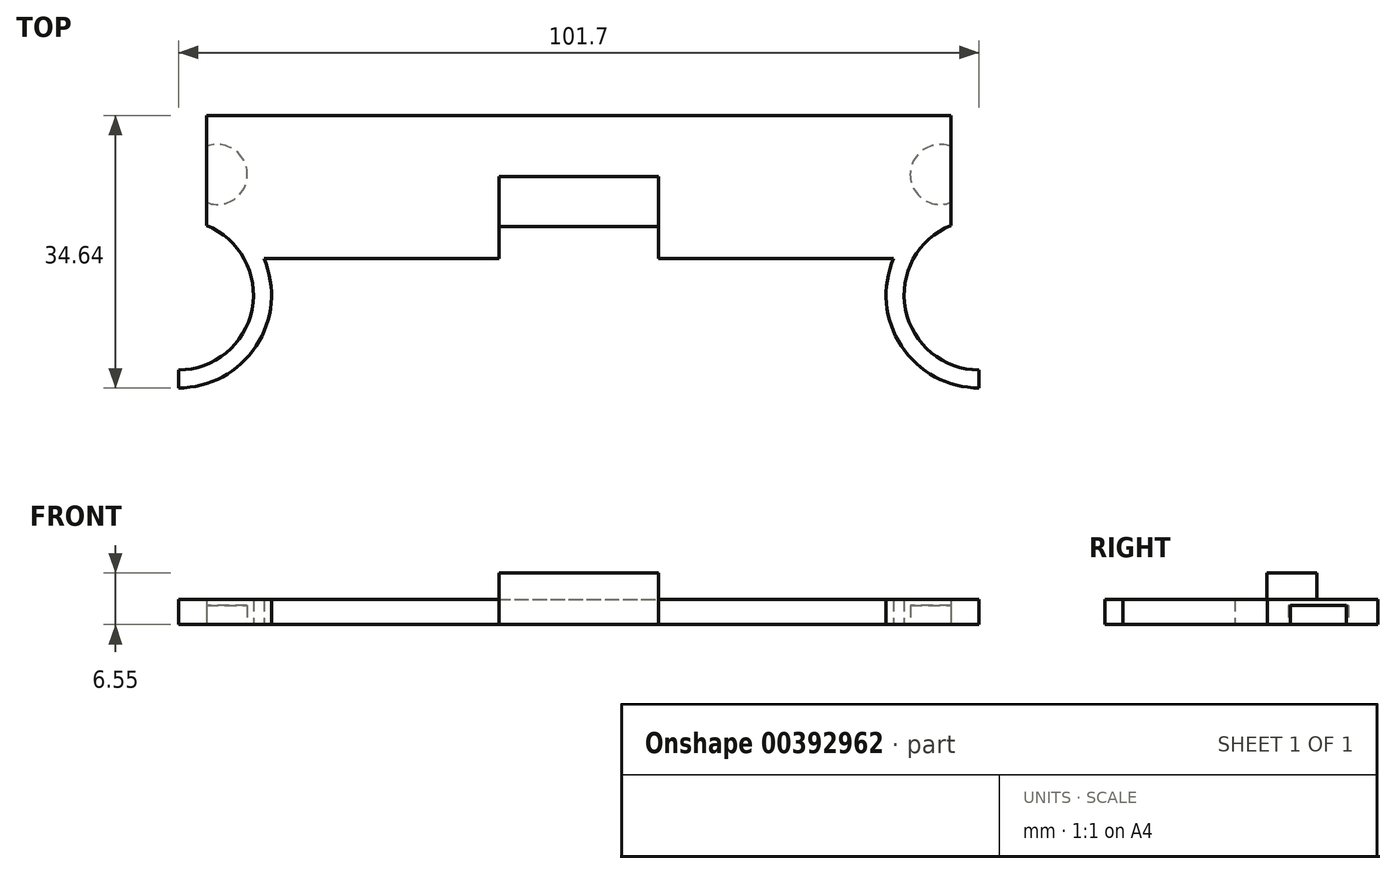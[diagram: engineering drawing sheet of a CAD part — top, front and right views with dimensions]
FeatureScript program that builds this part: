
annotation { "Feature Type Name" : "Feature", "Feature Type Description" : "" }
export const myFeature = defineFeature(function(context is Context, id is Id, definition is map)
    precondition{}
    {
        {
            var Q0;
            Q0=qCreatedBy(makeId("Top.planeOp"),FACE);
            var sketch = newSketch(context, id + "F0", { "sketchPlane" : qUnion([Q0])});
            skLineSegment(sketch, "E0.bottom", {"start": v(-47.29, 18.16) * mm, "end": v(47.29, 18.16) * mm});
            skLineSegment(sketch, "E0.top", {"start": v(-40, 0) * mm, "end": v(-10.16, 0) * mm});
            skLineSegment(sketch, "E0.left", {"start": v(-47.29, 18.16) * mm, "end": v(-47.29, 4.17) * mm});
            skLineSegment(sketch, "E0.right", {"start": v(47.29, 18.16) * mm, "end": v(47.29, 4.17) * mm});
            skArc(sketch, "E1", {"start": v(-50.85, -14.19) * mm, "mid": v(-41.5, -6.48) * mm, "end": v(-47.29, 4.17) * mm});
            skArc(sketch, "E2", {"start": v(-50.85, -16.48) * mm, "mid": v(-40.99, -11.16) * mm, "end": v(-40, 0) * mm});
            skLineSegment(sketch, "E3", {"start": v(-50.85, -14.19) * mm, "end": v(-50.85, -16.48) * mm});
            skArc(sketch, "E4.MirrorCS", {"start": v(50.85, -16.48) * mm, "mid": v(40.99, -11.16) * mm, "end": v(40, 0) * mm});
            skArc(sketch, "E5.MirrorCS", {"start": v(50.85, -14.19) * mm, "mid": v(41.5, -6.48) * mm, "end": v(47.29, 4.17) * mm});
            skLineSegment(sketch, "E6.MirrorCS", {"start": v(50.85, -14.19) * mm, "end": v(50.85, -16.48) * mm});
            skPoint(sketch, "E7.orphan", {"position": v(47.29, 0) * mm});
            skLineSegment(sketch, "E8.top", {"start": v(-10.16, 4.05) * mm, "end": v(10.16, 4.05) * mm});
            skLineSegment(sketch, "E8.left", {"start": v(-10.16, 0) * mm, "end": v(-10.16, 4.05) * mm});
            skLineSegment(sketch, "E8.right", {"start": v(10.16, 0) * mm, "end": v(10.16, 4.05) * mm});
            skLineSegment(sketch, "E9.trimOffspring", {"start": v(10.16, 0) * mm, "end": v(40, 0) * mm});
            skSolve(sketch);
        }
        {
            var Q0;
            Q0=qSketchRegion(id+"F0",true);
            extrude(context, id + "F1", {"entities" : qUnion([Q0]), "depth" : 3.17 * mm});
        }
        {
            var Q0;
            Q0=makeQuery(id+"F1.opExtrude","CAP_FACE",FACE,{"disambiguationData":[OSD([sQuery(id+"F0.wireOp",EDGE,"E0.bottom"),sQuery(id+"F0.wireOp",EDGE,"E0.top"),sQuery(id+"F0.wireOp",EDGE,"E0.left"),sQuery(id+"F0.wireOp",EDGE,"E0.right"),sQuery(id+"F0.wireOp",EDGE,"E1"),sQuery(id+"F0.wireOp",EDGE,"E2"),sQuery(id+"F0.wireOp",EDGE,"E3"),sQuery(id+"F0.wireOp",EDGE,"E4.MirrorCS"),sQuery(id+"F0.wireOp",EDGE,"E5.MirrorCS"),sQuery(id+"F0.wireOp",EDGE,"E6.MirrorCS"),sQuery(id+"F0.wireOp",EDGE,"E8.top"),sQuery(id+"F0.wireOp",EDGE,"E8.left"),sQuery(id+"F0.wireOp",EDGE,"E8.right"),sQuery(id+"F0.wireOp",EDGE,"E9.trimOffspring")])],"isStart":true});
            var sketch = newSketch(context, id + "F2", { "sketchPlane" : qUnion([Q0])});
            skArc(sketch, "E10", {"start": v(-47.29, -14.2) * mm, "mid": v(-42.1, -10.64) * mm, "end": v(-47.29, -7.1) * mm});
            skLineSegment(sketch, "E11", {"start": v(-47.29, -7.1) * mm, "end": v(-47.29, -14.2) * mm});
            skArc(sketch, "E12.MirrorCS", {"start": v(47.29, -14.2) * mm, "mid": v(42.1, -10.64) * mm, "end": v(47.29, -7.1) * mm});
            skLineSegment(sketch, "E13.MirrorCS", {"start": v(47.29, -7.1) * mm, "end": v(47.29, -14.2) * mm});
            skSolve(sketch);
        }
        {
            var Q0;
            Q0=qSketchRegion(id+"F2",true);
            extrude(context, id + "F3", {"entities" : qUnion([Q0]), "operationType" : NewBodyOperationType.REMOVE, "oppositeDirection" : true, "depth" : 2.41 * mm});
        }
        {
            var Q0;
            Q0=makeQuery(id+"F1.opExtrude","CAP_FACE",FACE,{"disambiguationData":[OSD([sQuery(id+"F0.wireOp",EDGE,"E0.bottom"),sQuery(id+"F0.wireOp",EDGE,"E0.top"),sQuery(id+"F0.wireOp",EDGE,"E0.left"),sQuery(id+"F0.wireOp",EDGE,"E0.right"),sQuery(id+"F0.wireOp",EDGE,"E1"),sQuery(id+"F0.wireOp",EDGE,"E2"),sQuery(id+"F0.wireOp",EDGE,"E3"),sQuery(id+"F0.wireOp",EDGE,"E4.MirrorCS"),sQuery(id+"F0.wireOp",EDGE,"E5.MirrorCS"),sQuery(id+"F0.wireOp",EDGE,"E6.MirrorCS"),sQuery(id+"F0.wireOp",EDGE,"E8.top"),sQuery(id+"F0.wireOp",EDGE,"E8.left"),sQuery(id+"F0.wireOp",EDGE,"E8.right"),sQuery(id+"F0.wireOp",EDGE,"E9.trimOffspring")])],"isStart":false});
            var sketch = newSketch(context, id + "F4", { "sketchPlane" : qUnion([Q0])});
            skLineSegment(sketch, "E14.bottom", {"start": v(-10.16, 4.05) * mm, "end": v(10.16, 4.05) * mm});
            skLineSegment(sketch, "E14.top", {"start": v(-10.16, 10.4) * mm, "end": v(10.16, 10.4) * mm});
            skLineSegment(sketch, "E14.left", {"start": v(-10.16, 4.05) * mm, "end": v(-10.16, 10.4) * mm});
            skLineSegment(sketch, "E14.right", {"start": v(10.16, 4.05) * mm, "end": v(10.16, 10.4) * mm});
            skSolve(sketch);
        }
        {
            var Q0;
            Q0=qSketchRegion(id+"F4",true);
            extrude(context, id + "F5", {"entities" : qUnion([Q0]), "operationType" : NewBodyOperationType.ADD, "depth" : 3.38 * mm});
        }
    });
